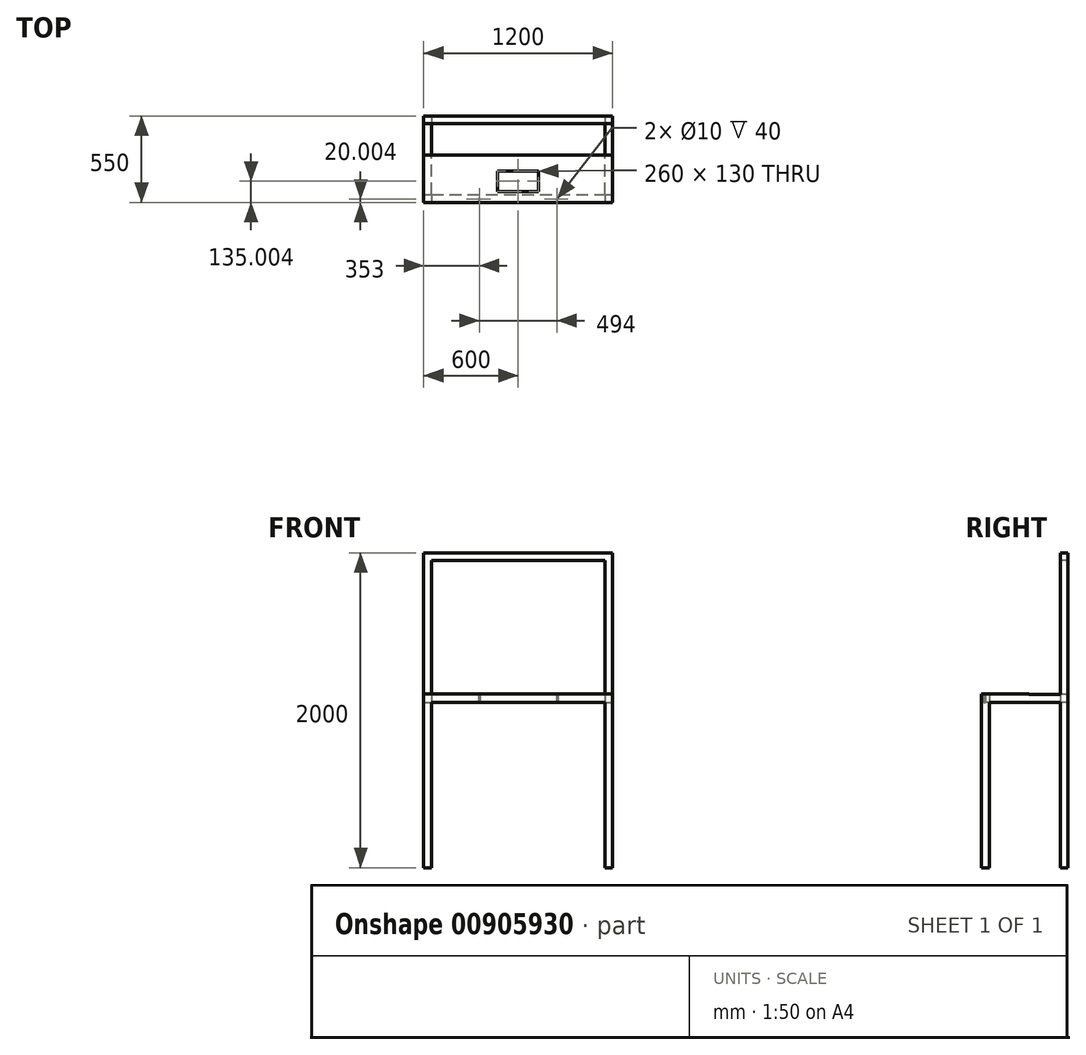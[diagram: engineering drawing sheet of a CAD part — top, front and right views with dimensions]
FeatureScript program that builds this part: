
annotation { "Feature Type Name" : "Feature", "Feature Type Description" : "" }
export const myFeature = defineFeature(function(context is Context, id is Id, definition is map)
    precondition{}
    {
        {
            var Q0;
            Q0=qCreatedBy(makeId("Right.planeOp"),FACE);
            var sketch = newSketch(context, id + "F0", { "sketchPlane" : qUnion([Q0])});
            skLineSegment(sketch, "E0.top", {"start": v(-112.44, -990.8) * mm, "end": v(-62.44, -990.8) * mm});
            skLineSegment(sketch, "E0.left", {"start": v(-112.44, 109.2) * mm, "end": v(-112.44, -990.8) * mm});
            skLineSegment(sketch, "E1", {"start": v(-112.44, 109.2) * mm, "end": v(387.56, 109.2) * mm});
            skLineSegment(sketch, "E2", {"start": v(387.56, 109.2) * mm, "end": v(387.56, 1009.2) * mm});
            skLineSegment(sketch, "E3", {"start": v(387.56, 1009.2) * mm, "end": v(437.56, 1009.2) * mm});
            skLineSegment(sketch, "E4", {"start": v(437.56, 1009.2) * mm, "end": v(437.56, -990.8) * mm});
            skLineSegment(sketch, "E5.top", {"start": v(-62.44, 59.2) * mm, "end": v(387.56, 59.2) * mm});
            skLineSegment(sketch, "E5.left", {"start": v(-62.44, -990.8) * mm, "end": v(-62.44, 59.2) * mm});
            skLineSegment(sketch, "E5.right", {"start": v(387.56, -990.8) * mm, "end": v(387.56, 59.2) * mm});
            skLineSegment(sketch, "E6.trimOffspring", {"start": v(387.56, -990.8) * mm, "end": v(437.56, -990.8) * mm});
            skSolve(sketch);
        }
        {
            var Q0;
            Q0 = qSketchRegion(id + "F0", true);
            extrude(context, id + "F1", {"entities" : qUnion([Q0]), "oppositeDirection" : true, "depth" : 1200 * mm, "offsetDistance" : 25 * mm});
        }
        {
            var Q0;
            Q0=makeQuery(id+"F1.opExtrude","SWEPT_FACE",FACE,{"disambiguationData":[OSD([sQuery(id+"F0.wireOp",EDGE,"E0.left")])]});
            var sketch = newSketch(context, id + "F2", { "sketchPlane" : qUnion([Q0])});
            skLineSegment(sketch, "E7.bottom", {"start": v(-1150, 59.2) * mm, "end": v(-50, 59.2) * mm});
            skLineSegment(sketch, "E7.top", {"start": v(-1150, -990.8) * mm, "end": v(-50, -990.8) * mm});
            skLineSegment(sketch, "E7.left", {"start": v(-1150, 59.2) * mm, "end": v(-1150, -990.8) * mm});
            skLineSegment(sketch, "E7.right", {"start": v(-50, 59.2) * mm, "end": v(-50, -990.8) * mm});
            skSolve(sketch);
        }
        {
            var Q0;
            Q0 = qSketchRegion(id + "F2", true);
            extrude(context, id + "F3", {"entities" : qUnion([Q0]), "operationType" : NewBodyOperationType.REMOVE, "endBound" : BoundingType.THROUGH_ALL, "oppositeDirection" : true, "depth" : 25 * mm, "offsetDistance" : 25 * mm});
        }
        {
            var Q0;
            Q0=makeQuery(id+"F1.opExtrude","SWEPT_FACE",FACE,{"disambiguationData":[OSD([sQuery(id+"F0.wireOp",EDGE,"E2")])]});
            var sketch = newSketch(context, id + "F4", { "sketchPlane" : qUnion([Q0])});
            skLineSegment(sketch, "E8.bottom", {"start": v(-1150, 959.2) * mm, "end": v(-50, 959.2) * mm});
            skLineSegment(sketch, "E8.top", {"start": v(-1150, 109.2) * mm, "end": v(-50, 109.2) * mm});
            skLineSegment(sketch, "E8.left", {"start": v(-1150, 959.2) * mm, "end": v(-1150, 109.2) * mm});
            skLineSegment(sketch, "E8.right", {"start": v(-50, 959.2) * mm, "end": v(-50, 109.2) * mm});
            skSolve(sketch);
        }
        {
            var Q0;
            Q0 = qSketchRegion(id + "F4", true);
            extrude(context, id + "F5", {"entities" : qUnion([Q0]), "operationType" : NewBodyOperationType.REMOVE, "endBound" : BoundingType.THROUGH_ALL, "oppositeDirection" : true, "depth" : 25 * mm, "offsetDistance" : 25 * mm});
        }
        {
            var Q0;
            Q0=makeQuery(id+"F3.boolean.opBoolean","MERGE",FACE,{"derivedFrom":[makeQuery(id+"F1.opExtrude","SWEPT_FACE",FACE,{"disambiguationData":[OSD([sQuery(id+"F0.wireOp",EDGE,"E5.top")])]})],"fromTools":[makeQuery(id+"F3.opExtrude","SWEPT_FACE",FACE,{"disambiguationData":[OSD([sQuery(id+"F2.wireOp",EDGE,"E7.bottom")])]})]});
            var sketch = newSketch(context, id + "F6", { "sketchPlane" : qUnion([Q0])});
            skCircle(sketch, "E9", {"center": v(-847, 92.44) * mm, "radius": 5 * mm});
            skCircle(sketch, "E10", {"center": v(-353, 92.44) * mm, "radius": 5 * mm});
            skSolve(sketch);
        }
        {
            var Q0;
            Q0 = qSketchRegion(id + "F6", true);
            extrude(context, id + "F7", {"entities" : qUnion([Q0]), "operationType" : NewBodyOperationType.REMOVE, "oppositeDirection" : true, "depth" : 40 * mm, "offsetDistance" : 25 * mm});
        }
        {
            var Q0;
            Q0=makeQuery(id+"F3.boolean.opBoolean","MERGE",FACE,{"derivedFrom":[makeQuery(id+"F1.opExtrude","SWEPT_FACE",FACE,{"disambiguationData":[OSD([sQuery(id+"F0.wireOp",EDGE,"E5.top")])]})],"fromTools":[makeQuery(id+"F3.opExtrude","SWEPT_FACE",FACE,{"disambiguationData":[OSD([sQuery(id+"F2.wireOp",EDGE,"E7.bottom")])]})]});
            var sketch = newSketch(context, id + "F8", { "sketchPlane" : qUnion([Q0])});
            skLineSegment(sketch, "E11.bottom", {"start": v(-1150, 62.44) * mm, "end": v(-50, 62.44) * mm});
            skLineSegment(sketch, "E11.top", {"start": v(-1150, -387.56) * mm, "end": v(-50, -387.56) * mm});
            skLineSegment(sketch, "E11.left", {"start": v(-1150, 62.44) * mm, "end": v(-1150, -387.56) * mm});
            skLineSegment(sketch, "E11.right", {"start": v(-50, 62.44) * mm, "end": v(-50, -387.56) * mm});
            skSolve(sketch);
        }
        {
            var Q0;
            Q0 = qSketchRegion(id + "F8", true);
            extrude(context, id + "F9", {"entities" : qUnion([Q0]), "operationType" : NewBodyOperationType.REMOVE, "endBound" : BoundingType.THROUGH_ALL, "oppositeDirection" : true, "depth" : 25 * mm, "offsetDistance" : 25 * mm});
        }
        {
            var Q0;
            {var subQ7=sQuery(id+"F0.wireOp",EDGE,"E1");var subQ8=sQuery(id+"F0.wireOp",EDGE,"E0.left");var subQ10=makeQuery(id+"F1.opExtrude","SWEPT_FACE",FACE,{"disambiguationData":[OSD([subQ7])]});Q0=makeQuery(id+"F9.boolean.opBoolean","SPLIT",FACE,{"disambiguationData":[TD([makeQuery(id+"F1.opExtrude","SWEPT_FACE",FACE,{"disambiguationData":[OSD([subQ8])]})])],"derivedFrom":makeQuery(id+"F5.boolean.opBoolean","MERGE",FACE,{"derivedFrom":[subQ10],"fromTools":[makeQuery(id+"F5.opExtrude","SWEPT_FACE",FACE,{"disambiguationData":[OSD([sQuery(id+"F4.wireOp",EDGE,"E8.top")])]})]})});}
            var sketch = newSketch(context, id + "F10", { "sketchPlane" : qUnion([Q0])});
            skLineSegment(sketch, "E12.bottom", {"start": v(-1200, -112.44) * mm, "end": v(0, -112.44) * mm});
            skLineSegment(sketch, "E12.top", {"start": v(-1200, 187.56) * mm, "end": v(0, 187.56) * mm});
            skLineSegment(sketch, "E12.left", {"start": v(-1200, -112.44) * mm, "end": v(-1200, 187.56) * mm});
            skLineSegment(sketch, "E12.right", {"start": v(0, -112.44) * mm, "end": v(0, 187.56) * mm});
            skSolve(sketch);
        }
        {
            var Q0;
            Q0 = qSketchRegion(id + "F10", true);
            extrude(context, id + "F11", {"entities" : qUnion([Q0]), "operationType" : NewBodyOperationType.ADD, "depth" : 4 * mm, "offsetDistance" : 25 * mm});
        }
        {
            var Q0;
            Q0=makeQuery(id+"F11.opExtrude","CAP_FACE",FACE,{"disambiguationData":[OSD([sQuery(id+"F10.wireOp",EDGE,"E12.bottom"),sQuery(id+"F10.wireOp",EDGE,"E12.top"),sQuery(id+"F10.wireOp",EDGE,"E12.left"),sQuery(id+"F10.wireOp",EDGE,"E12.right")])],"isStart":false});
            var sketch = newSketch(context, id + "F12", { "sketchPlane" : qUnion([Q0])});
            skLineSegment(sketch, "E13.bottom", {"start": v(-730, 87.56) * mm, "end": v(-470, 87.56) * mm});
            skLineSegment(sketch, "E13.top", {"start": v(-730, -42.44) * mm, "end": v(-470, -42.44) * mm});
            skLineSegment(sketch, "E13.left", {"start": v(-730, 87.56) * mm, "end": v(-730, -42.44) * mm});
            skLineSegment(sketch, "E13.right", {"start": v(-470, 87.56) * mm, "end": v(-470, -42.44) * mm});
            skSolve(sketch);
        }
        {
            var Q0;
            Q0 = qSketchRegion(id + "F12", true);
            extrude(context, id + "F13", {"entities" : qUnion([Q0]), "operationType" : NewBodyOperationType.REMOVE, "oppositeDirection" : true, "depth" : 4 * mm, "offsetDistance" : 25 * mm});
        }
    });
